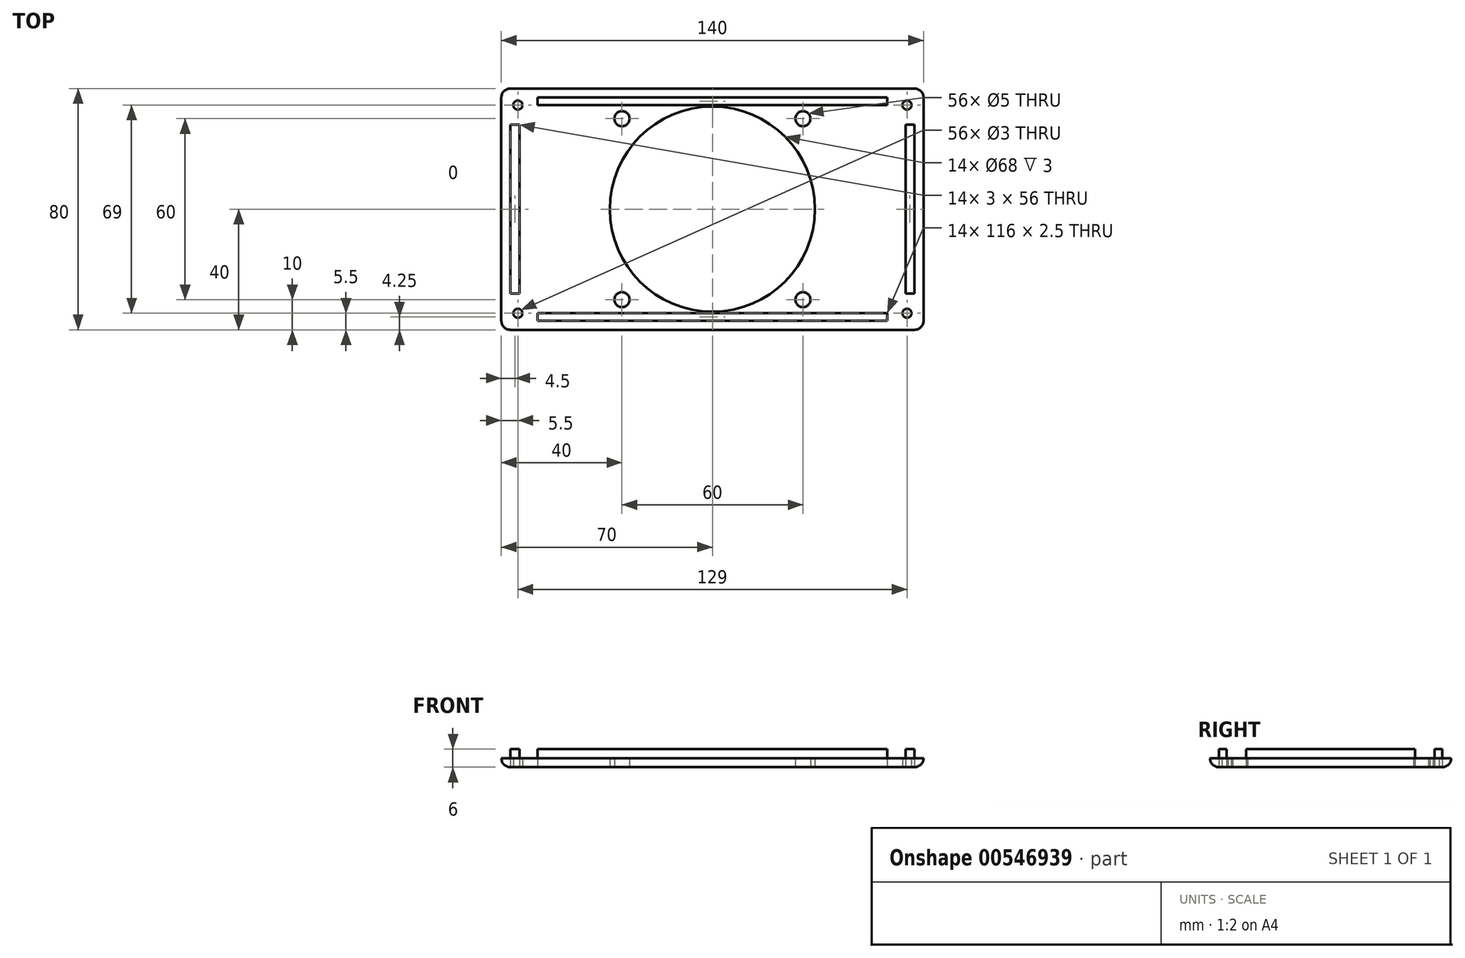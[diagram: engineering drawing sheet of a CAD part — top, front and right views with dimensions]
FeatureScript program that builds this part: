
annotation { "Feature Type Name" : "Feature", "Feature Type Description" : "" }
export const myFeature = defineFeature(function(context is Context, id is Id, definition is map)
    precondition{}
    {
        {
            var Q0;
            Q0=qCreatedBy(makeId("Top.planeOp"),FACE);
            var sketch = newSketch(context, id + "F0", { "sketchPlane" : qUnion([Q0])});
            skLineSegment(sketch, "E0", {"start": v(0, 0) * mm, "end": v(0, 80) * mm});
            skLineSegment(sketch, "E1", {"start": v(0, 80) * mm, "end": v(140, 80) * mm});
            skLineSegment(sketch, "E2", {"start": v(140, 80) * mm, "end": v(140, 0) * mm});
            skLineSegment(sketch, "E3", {"start": v(140, 0) * mm, "end": v(0, 0) * mm});
            skLineSegment(sketch, "E4.0", {"start": v(0, 74.5) * mm, "end": v(5.5, 74.5) * mm, "construction": true});
            skLineSegment(sketch, "E5.0", {"start": v(140, 5.5) * mm, "end": v(134.5, 5.5) * mm, "construction": true});
            skLineSegment(sketch, "E6.0", {"start": v(5.5, 0) * mm, "end": v(5.5, 5.5) * mm, "construction": true});
            skLineSegment(sketch, "E7.0", {"start": v(134.5, 80) * mm, "end": v(134.5, 74.5) * mm, "construction": true});
            skLineSegment(sketch, "E8.trimOffspring", {"start": v(5.5, 74.5) * mm, "end": v(5.5, 80) * mm, "construction": true});
            skLineSegment(sketch, "E9.trimOffspring", {"start": v(134.5, 74.5) * mm, "end": v(140, 74.5) * mm, "construction": true});
            skLineSegment(sketch, "E10.trimOffspring", {"start": v(134.5, 5.5) * mm, "end": v(134.5, 0) * mm, "construction": true});
            skLineSegment(sketch, "E11.trimOffspring", {"start": v(5.5, 5.5) * mm, "end": v(0, 5.5) * mm, "construction": true});
            skCircle(sketch, "E12", {"center": v(5.5, 74.5) * mm, "radius": 1.5 * mm});
            skCircle(sketch, "E13", {"center": v(134.5, 74.5) * mm, "radius": 1.5 * mm});
            skCircle(sketch, "E14", {"center": v(134.5, 5.5) * mm, "radius": 1.5 * mm});
            skCircle(sketch, "E15", {"center": v(5.5, 5.5) * mm, "radius": 1.5 * mm});
            skLineSegment(sketch, "E16.0", {"start": v(70, 0) * mm, "end": v(70, 80) * mm, "construction": true});
            skLineSegment(sketch, "E17.0", {"start": v(0, 40) * mm, "end": v(140, 40) * mm, "construction": true});
            skCircle(sketch, "E18", {"center": v(70, 40) * mm, "radius": 34 * mm});
            skLineSegment(sketch, "E19.0", {"start": v(40, 10) * mm, "end": v(100, 10) * mm, "construction": true});
            skLineSegment(sketch, "E20.0", {"start": v(40, 70) * mm, "end": v(100, 70) * mm, "construction": true});
            skLineSegment(sketch, "E21.0", {"start": v(100, 10) * mm, "end": v(100, 70) * mm, "construction": true});
            skLineSegment(sketch, "E22.0", {"start": v(40, 10) * mm, "end": v(40, 70) * mm, "construction": true});
            skCircle(sketch, "E23", {"center": v(40, 70) * mm, "radius": 2.5 * mm});
            skCircle(sketch, "E24", {"center": v(40, 10) * mm, "radius": 2.5 * mm});
            skCircle(sketch, "E25", {"center": v(100, 70) * mm, "radius": 2.5 * mm});
            skLineSegment(sketch, "E26.0", {"start": v(12, 3) * mm, "end": v(12, 5.5) * mm});
            skLineSegment(sketch, "E27.0", {"start": v(128, 77) * mm, "end": v(128, 74.5) * mm});
            skLineSegment(sketch, "E28.0", {"start": v(12, 77) * mm, "end": v(128, 77) * mm});
            skLineSegment(sketch, "E29.0", {"start": v(12, 74.5) * mm, "end": v(128, 74.5) * mm});
            skLineSegment(sketch, "E30.0", {"start": v(128, 3) * mm, "end": v(12, 3) * mm});
            skLineSegment(sketch, "E31.0", {"start": v(128, 5.5) * mm, "end": v(12, 5.5) * mm});
            skLineSegment(sketch, "E32.trimOffspring", {"start": v(128, 5.5) * mm, "end": v(128, 3) * mm});
            skLineSegment(sketch, "E33.trimOffspring", {"start": v(12, 74.5) * mm, "end": v(12, 77) * mm});
            skLineSegment(sketch, "E34.0", {"start": v(3, 12) * mm, "end": v(3, 68) * mm});
            skLineSegment(sketch, "E35.0", {"start": v(6, 12) * mm, "end": v(6, 68) * mm});
            skLineSegment(sketch, "E36.0", {"start": v(137, 68) * mm, "end": v(137, 12) * mm});
            skLineSegment(sketch, "E37.0", {"start": v(134, 68) * mm, "end": v(134, 12) * mm});
            skLineSegment(sketch, "E38.0", {"start": v(3, 68) * mm, "end": v(6, 68) * mm});
            skLineSegment(sketch, "E39.0", {"start": v(137, 12) * mm, "end": v(134, 12) * mm});
            skCircle(sketch, "E40", {"center": v(100, 10) * mm, "radius": 2.5 * mm});
            skLineSegment(sketch, "E41.trimOffspring", {"start": v(6, 12) * mm, "end": v(3, 12) * mm});
            skLineSegment(sketch, "E42.trimOffspring", {"start": v(134, 68) * mm, "end": v(137, 68) * mm});
            skSolve(sketch);
        }
        {
            var Q0;
            {var subQ1=sQuery(id+"F0.wireOp",EDGE,"E27.0");Q0=makeQuery(id+"F0.imprint","IMPRINT",FACE,{"disambiguationData":[TD([[makeQuery(id+"F0.imprint","IMPRINT",EDGE,{"derivedFrom":subQ1}),-1.0]])]});}
            var Q1;
            {var subQ1=sQuery(id+"F0.wireOp",EDGE,"E26.0");Q1=makeQuery(id+"F0.imprint","IMPRINT",FACE,{"disambiguationData":[TD([[makeQuery(id+"F0.imprint","IMPRINT",EDGE,{"derivedFrom":subQ1}),-1.0]])]});}
            var Q2;
            Q2=makeQuery(id+"F0.imprint","IMPRINT",FACE,{"disambiguationData":[TD([[makeQuery(id+"F0.imprint","IMPRINT",EDGE,{"derivedFrom":sQuery(id+"F0.wireOp",EDGE,"E34.0")}),-1.0]])]});
            var Q3;
            Q3=makeQuery(id+"F0.imprint","IMPRINT",FACE,{"disambiguationData":[TD([[makeQuery(id+"F0.imprint","IMPRINT",EDGE,{"derivedFrom":sQuery(id+"F0.wireOp",EDGE,"E36.0")}),-1.0]])]});
            extrude(context, id + "F1", {"entities" : qUnion([Q0, Q1, Q2, Q3]), "depth" : 6 * mm, "offsetDistance" : 25 * mm});
        }
        {
            var Q0;
            Q0=makeQuery(id+"F0.imprint","IMPRINT",FACE,{"disambiguationData":[TD([[makeQuery(id+"F0.imprint","IMPRINT",EDGE,{"derivedFrom":sQuery(id+"F0.wireOp",EDGE,"E0")}),-1.0]])]});
            extrude(context, id + "F2", {"entities" : qUnion([Q0]), "depth" : 3 * mm, "offsetDistance" : 25 * mm});
        }
        {
            var Q0;
            Q0=makeQuery(id+"F2.opExtrude","CAP_EDGE",EDGE,{"disambiguationData":[OSD([sQuery(id+"F0.wireOp",EDGE,"E2")])],"isStart":true});
            var Q1;
            Q1=makeQuery(id+"F2.opExtrude","SWEPT_EDGE",EDGE,{"disambiguationData":[OSD([sQuery(id+"F0.wireOp",EDGE,"E1"),sQuery(id+"F0.wireOp",EDGE,"E2")])]});
            var Q2;
            Q2=makeQuery(id+"F2.opExtrude","SWEPT_EDGE",EDGE,{"disambiguationData":[OSD([sQuery(id+"F0.wireOp",EDGE,"E0"),sQuery(id+"F0.wireOp",EDGE,"E3")])]});
            var Q3;
            Q3=makeQuery(id+"F2.opExtrude","SWEPT_EDGE",EDGE,{"disambiguationData":[OSD([sQuery(id+"F0.wireOp",EDGE,"E0"),sQuery(id+"F0.wireOp",EDGE,"E1")])]});
            var Q4;
            Q4=makeQuery(id+"F2.opExtrude","SWEPT_EDGE",EDGE,{"disambiguationData":[OSD([sQuery(id+"F0.wireOp",EDGE,"E2"),sQuery(id+"F0.wireOp",EDGE,"E3")])]});
            var Q5;
            Q5=makeQuery(id+"F2.opExtrude","CAP_EDGE",EDGE,{"disambiguationData":[OSD([sQuery(id+"F0.wireOp",EDGE,"E3")])],"isStart":true});
            var Q6;
            Q6=makeQuery(id+"F2.opExtrude","CAP_EDGE",EDGE,{"disambiguationData":[OSD([sQuery(id+"F0.wireOp",EDGE,"E1")])],"isStart":true});
            var Q7;
            Q7=makeQuery(id+"F2.opExtrude","CAP_EDGE",EDGE,{"disambiguationData":[OSD([sQuery(id+"F0.wireOp",EDGE,"E0")])],"isStart":true});
            fillet(context, id + "F3", {"entities" : qUnion([Q0, Q1, Q2, Q3, Q4, Q5, Q6, Q7]), "radius" : 3 * mm, "tangentPropagation" : true, "allowEdgeOverflow" : false});
        }
    });
